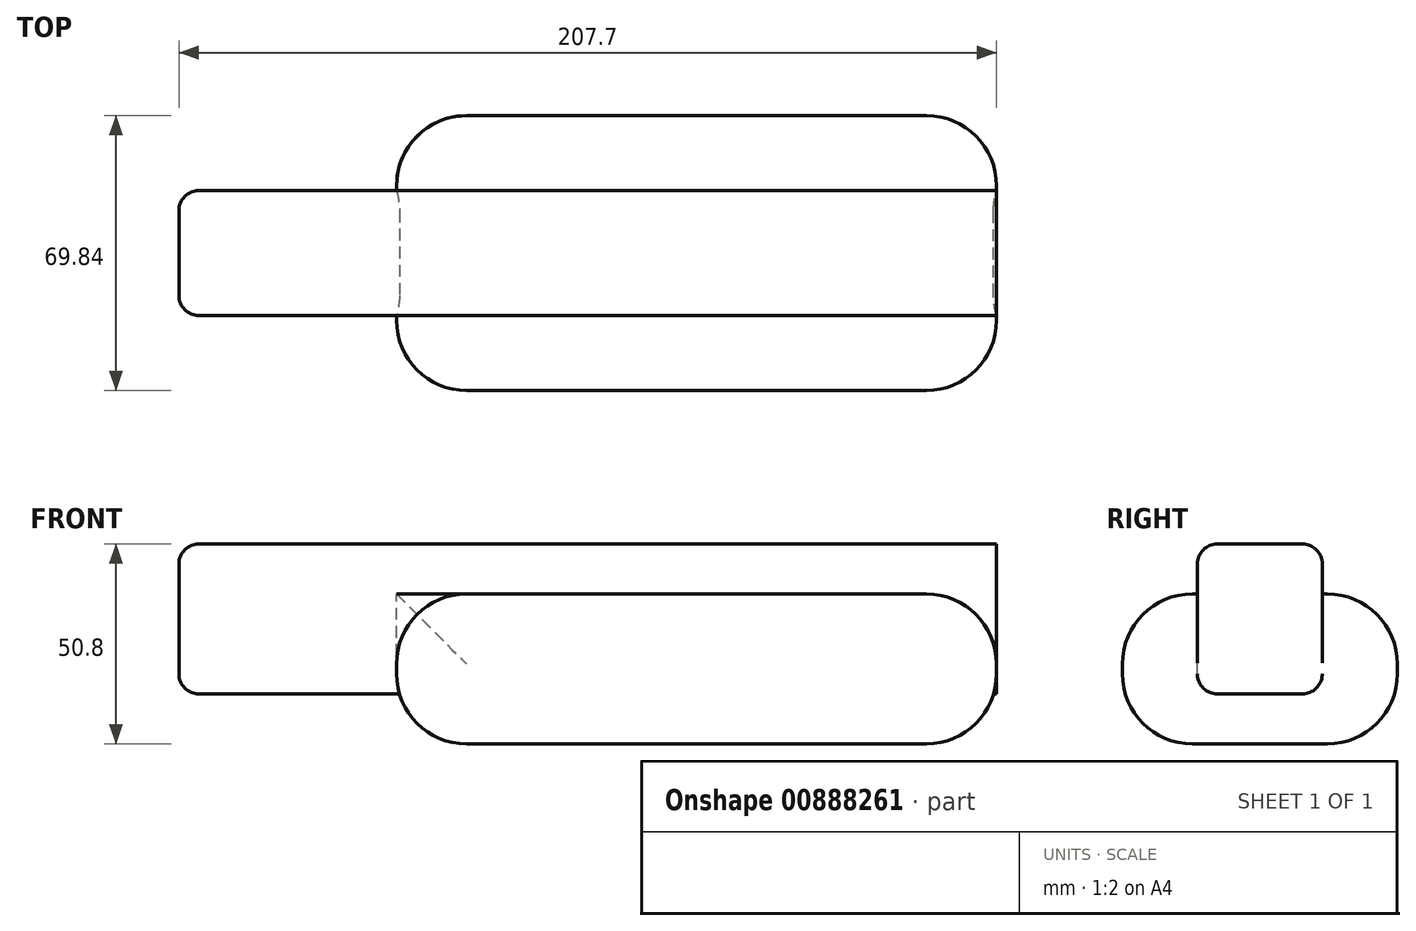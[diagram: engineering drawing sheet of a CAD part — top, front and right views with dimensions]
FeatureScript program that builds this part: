
annotation { "Feature Type Name" : "Feature", "Feature Type Description" : "" }
export const myFeature = defineFeature(function(context is Context, id is Id, definition is map)
    precondition{}
    {
        {
            var Q0;
            Q0=qCreatedBy(makeId("Top.planeOp"),FACE);
            var sketch = newSketch(context, id + "F0", { "sketchPlane" : qUnion([Q0])});
            skLineSegment(sketch, "E0.bottom", {"start": v(-101.7, 15.87) * mm, "end": v(114.2, 15.87) * mm});
            skLineSegment(sketch, "E0.top", {"start": v(-101.7, -15.87) * mm, "end": v(114.2, -15.87) * mm});
            skLineSegment(sketch, "E0.left", {"start": v(-101.7, 15.88) * mm, "end": v(-101.7, -15.87) * mm});
            skLineSegment(sketch, "E0.right", {"start": v(114.2, 15.88) * mm, "end": v(114.2, -15.87) * mm});
            skSolve(sketch);
        }
        {
            var Q0;
            Q0 = qSketchRegion(id + "F0", true);
            extrude(context, id + "F1", {"entities" : qUnion([Q0]), "depth" : 38.1 * mm, "offsetDistance" : 25.4 * mm});
        }
        {
            var Q0;
            Q0=makeQuery(id+"F1.opExtrude","CAP_EDGE",EDGE,{"disambiguationData":[OSD([sQuery(id+"F0.wireOp",EDGE,"E0.top")])],"isStart":false});
            var Q1;
            Q1=makeQuery(id+"F1.opExtrude","CAP_EDGE",EDGE,{"disambiguationData":[OSD([sQuery(id+"F0.wireOp",EDGE,"E0.bottom")])],"isStart":false});
            var Q2;
            Q2=makeQuery(id+"F1.opExtrude","CAP_EDGE",EDGE,{"disambiguationData":[OSD([sQuery(id+"F0.wireOp",EDGE,"E0.top")])],"isStart":true});
            var Q3;
            Q3=makeQuery(id+"F1.opExtrude","CAP_EDGE",EDGE,{"disambiguationData":[OSD([sQuery(id+"F0.wireOp",EDGE,"E0.bottom")])],"isStart":true});
            var Q4;
            Q4=makeQuery(id+"F1.opExtrude","CAP_EDGE",EDGE,{"disambiguationData":[OSD([sQuery(id+"F0.wireOp",EDGE,"E0.left")])],"isStart":false});
            var Q5;
            Q5=makeQuery(id+"F1.opExtrude","SWEPT_EDGE",EDGE,{"disambiguationData":[OSD([sQuery(id+"F0.wireOp",EDGE,"E0.bottom"),sQuery(id+"F0.wireOp",EDGE,"E0.left")])]});
            var Q6;
            Q6=makeQuery(id+"F1.opExtrude","CAP_EDGE",EDGE,{"disambiguationData":[OSD([sQuery(id+"F0.wireOp",EDGE,"E0.left")])],"isStart":true});
            var Q7;
            Q7=makeQuery(id+"F1.opExtrude","SWEPT_EDGE",EDGE,{"disambiguationData":[OSD([sQuery(id+"F0.wireOp",EDGE,"E0.top"),sQuery(id+"F0.wireOp",EDGE,"E0.left")])]});
            fillet(context, id + "F2", {"entities" : qUnion([Q0, Q1, Q2, Q3, Q4, Q5, Q6, Q7]), "radius" : 5.08 * mm, "tangentPropagation" : true, "allowEdgeOverflow" : false});
        }
        {
            var Q0;
            Q0=makeQuery(id+"F1.opExtrude","CAP_FACE",FACE,{"disambiguationData":[OSD([sQuery(id+"F0.wireOp",EDGE,"E0.bottom"),sQuery(id+"F0.wireOp",EDGE,"E0.top"),sQuery(id+"F0.wireOp",EDGE,"E0.left"),sQuery(id+"F0.wireOp",EDGE,"E0.right")])],"isStart":true});
            var sketch = newSketch(context, id + "F3", { "sketchPlane" : qUnion([Q0])});
            skLineSegment(sketch, "E1.bottom", {"start": v(-46.4, -34.93) * mm, "end": v(106, -34.93) * mm});
            skLineSegment(sketch, "E1.top", {"start": v(-46.4, 34.93) * mm, "end": v(106, 34.93) * mm});
            skLineSegment(sketch, "E1.left", {"start": v(-46.4, -34.93) * mm, "end": v(-46.4, 34.93) * mm});
            skLineSegment(sketch, "E1.right", {"start": v(106, -34.93) * mm, "end": v(106, 34.93) * mm});
            skSolve(sketch);
        }
        {
            var Q0;
            Q0 = qSketchRegion(id + "F3", true);
            extrude(context, id + "F4", {"entities" : qUnion([Q0]), "operationType" : NewBodyOperationType.ADD, "depth" : 12.7 * mm, "offsetDistance" : 25.4 * mm, "hasSecondDirection" : true, "secondDirectionOppositeDirection" : true, "secondDirectionDepth" : 25.4 * mm});
        }
        {
            var Q0;
            {var subQ0=sQuery(id+"F3.wireOp",EDGE,"E1.left");Q0=makeQuery(id+"F4.boolean.opBoolean","SPLIT",EDGE,{"disambiguationData":[TD([makeQuery(id+"F1.opExtrude","SWEPT_FACE",FACE,{"disambiguationData":[OSD([sQuery(id+"F0.wireOp",EDGE,"E0.top")])]})])],"derivedFrom":makeQuery(id+"F4.opExtrude","CAP_EDGE",EDGE,{"disambiguationData":[OSD([subQ0])],"isStart":true})});}
            var Q1;
            Q1=makeQuery(id+"F4.opExtrude","CAP_EDGE",EDGE,{"disambiguationData":[OSD([sQuery(id+"F3.wireOp",EDGE,"E1.top")])],"isStart":true});
            var Q2;
            Q2=makeQuery(id+"F4.opExtrude","SWEPT_EDGE",EDGE,{"disambiguationData":[OSD([sQuery(id+"F3.wireOp",EDGE,"E1.top"),sQuery(id+"F3.wireOp",EDGE,"E1.left")])]});
            var Q3;
            Q3=makeQuery(id+"F4.opExtrude","CAP_EDGE",EDGE,{"disambiguationData":[OSD([sQuery(id+"F3.wireOp",EDGE,"E1.top")])],"isStart":false});
            var Q4;
            Q4=makeQuery(id+"F4.opExtrude","CAP_EDGE",EDGE,{"disambiguationData":[OSD([sQuery(id+"F3.wireOp",EDGE,"E1.left")])],"isStart":false});
            var Q5;
            Q5=makeQuery(id+"F4.opExtrude","SWEPT_EDGE",EDGE,{"disambiguationData":[OSD([sQuery(id+"F3.wireOp",EDGE,"E1.top"),sQuery(id+"F3.wireOp",EDGE,"E1.right")])]});
            var Q6;
            {var subQ0=sQuery(id+"F3.wireOp",EDGE,"E1.right");var subQ3=sQuery(id+"F0.wireOp",EDGE,"E0.top");Q6=makeQuery(id+"F4.boolean.opBoolean","SPLIT",EDGE,{"disambiguationData":[TD([makeQuery(id+"F1.opExtrude","SWEPT_FACE",FACE,{"disambiguationData":[OSD([subQ3])]})])],"derivedFrom":makeQuery(id+"F4.opExtrude","CAP_EDGE",EDGE,{"disambiguationData":[OSD([subQ0])],"isStart":true})});}
            var Q7;
            Q7=makeQuery(id+"F4.opExtrude","SWEPT_FACE",FACE,{"disambiguationData":[OSD([sQuery(id+"F3.wireOp",EDGE,"E1.bottom")])]});
            var Q8;
            {var subQ1=sQuery(id+"F3.wireOp",EDGE,"E1.right");var subQ3=sQuery(id+"F0.wireOp",EDGE,"E0.bottom");Q8=makeQuery(id+"F4.boolean.opBoolean","SPLIT",EDGE,{"disambiguationData":[TD([makeQuery(id+"F1.opExtrude","SWEPT_FACE",FACE,{"disambiguationData":[OSD([subQ3])]})])],"derivedFrom":makeQuery(id+"F4.opExtrude","CAP_EDGE",EDGE,{"disambiguationData":[OSD([subQ1])],"isStart":true})});}
            var Q9;
            Q9=makeQuery(id+"F4.opExtrude","CAP_EDGE",EDGE,{"disambiguationData":[OSD([sQuery(id+"F3.wireOp",EDGE,"E1.right")])],"isStart":false});
            fillet(context, id + "F5", {"entities" : qUnion([Q0, Q1, Q2, Q3, Q4, Q5, Q6, Q7, Q8, Q9]), "radius" : 17.78 * mm, "tangentPropagation" : true, "allowEdgeOverflow" : false});
        }
        {
            var Q0;
            Q0=makeQuery(id+"F1.opExtrude","SWEPT_FACE",FACE,{"disambiguationData":[OSD([sQuery(id+"F0.wireOp",EDGE,"E0.right")])]});
            extrude(context, id + "F6", {"entities" : qUnion([Q0]), "operationType" : NewBodyOperationType.REMOVE, "oppositeDirection" : true, "depth" : 8.2 * mm, "offsetDistance" : 25.4 * mm});
        }
    });
